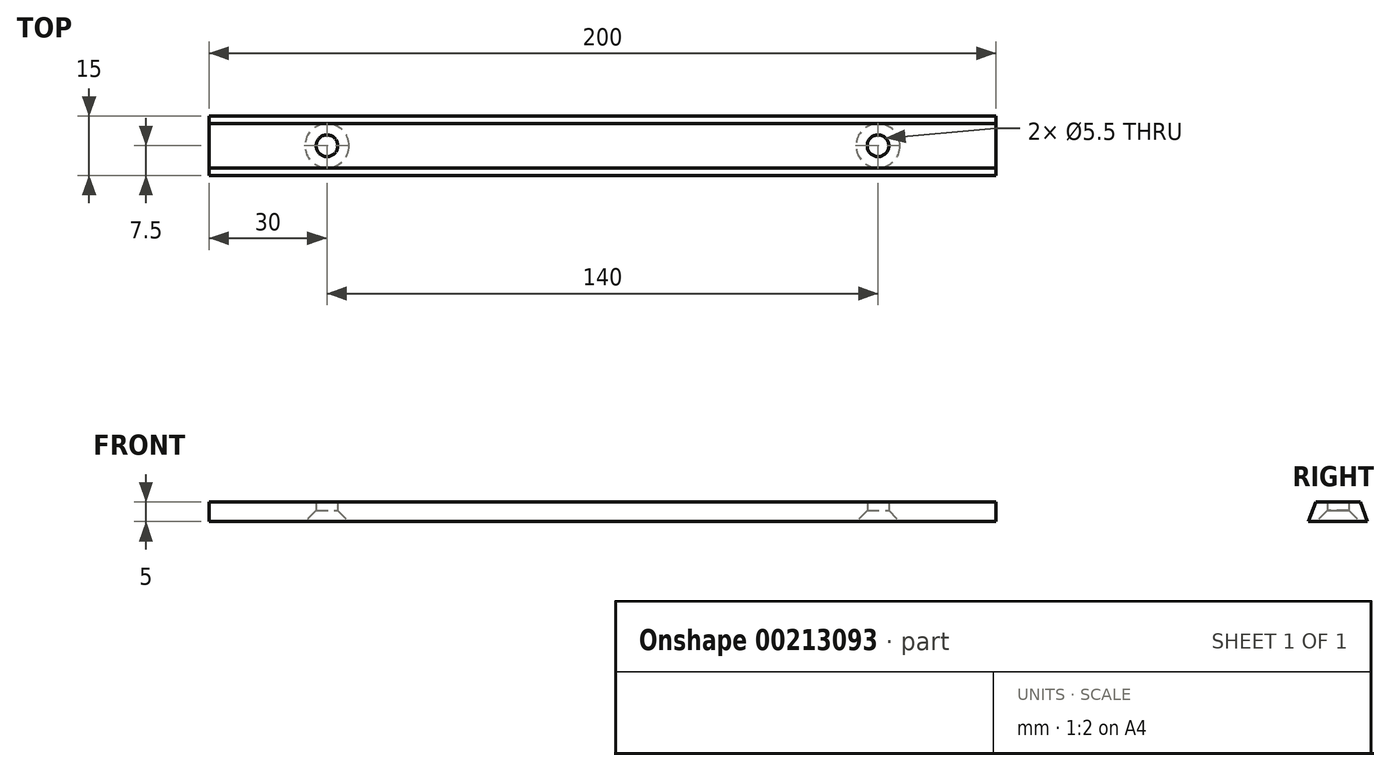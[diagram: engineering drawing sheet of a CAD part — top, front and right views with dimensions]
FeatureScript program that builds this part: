
annotation { "Feature Type Name" : "Feature", "Feature Type Description" : "" }
export const myFeature = defineFeature(function(context is Context, id is Id, definition is map)
    precondition{}
    {
        {
            var Q0;
            Q0=qCreatedBy(makeId("Right.planeOp"),FACE);
            var sketch = newSketch(context, id + "F0", { "sketchPlane" : qUnion([Q0])});
            skLineSegment(sketch, "E0", {"start": v(0, 0) * mm, "end": v(15, 0) * mm});
            skLineSegment(sketch, "E1", {"start": v(15, 0) * mm, "end": v(13.18, 5) * mm});
            skLineSegment(sketch, "E2", {"start": v(13.18, 5) * mm, "end": v(1.82, 5) * mm});
            skLineSegment(sketch, "E3", {"start": v(0, 0) * mm, "end": v(1.82, 5) * mm});
            skSolve(sketch);
        }
        {
            var Q0;
            Q0 = qSketchRegion(id + "F0", true);
            extrude(context, id + "F1", {"entities" : qUnion([Q0]), "depth" : 200 * mm});
        }
        {
            var Q0;
            Q0=qCreatedBy(makeId("Top.planeOp"),FACE);
            var sketch = newSketch(context, id + "F2", { "sketchPlane" : qUnion([Q0])});
            skPoint(sketch, "E4", {"position": v(30, 7.5) * mm});
            skPoint(sketch, "E5", {"position": v(170, 7.5) * mm});
            skSolve(sketch);
        }
        {
            var Q0;
            Q0=sQuery(id+"F2.wireOp",VERTEX,"E4");
            var Q1;
            Q1=sQuery(id+"F2.wireOp",VERTEX,"E5");
            var Q2;
            Q2=makeQuery(id+"F1.opExtrude","SWEPT_BODY",BODY,{"disambiguationData":[OSD([sQuery(id+"F0.wireOp",EDGE,"E0"),sQuery(id+"F0.wireOp",EDGE,"E1"),sQuery(id+"F0.wireOp",EDGE,"E2"),sQuery(id+"F0.wireOp",EDGE,"E3")])]});
            hole(context, id + "F3", {"style" : HoleStyle.C_SINK, "endStyle" : HoleEndStyle.THROUGH, "oppositeDirection" : true, "standardTappedOrClearance" : lookupTablePath({ "standard" : "ISO", "fit" : "Normal", "size" : "M5", "type" : "Clearance" }), "standardBlindInLast" : lookupTablePath({ "fit" : "Standard", "standard" : "ISO", "size" : "M5", "type" : "Clearance" }), "holeDiameter" : 5.5 * mm, "cSinkDiameter" : 11.2 * mm, "cSinkAngle" : 90 * degree, "startFromSketch" : true, "locations" : qUnion([Q0, Q1]), "scope" : qUnion([Q2]), "isTappedThrough" : true});
        }
    });
